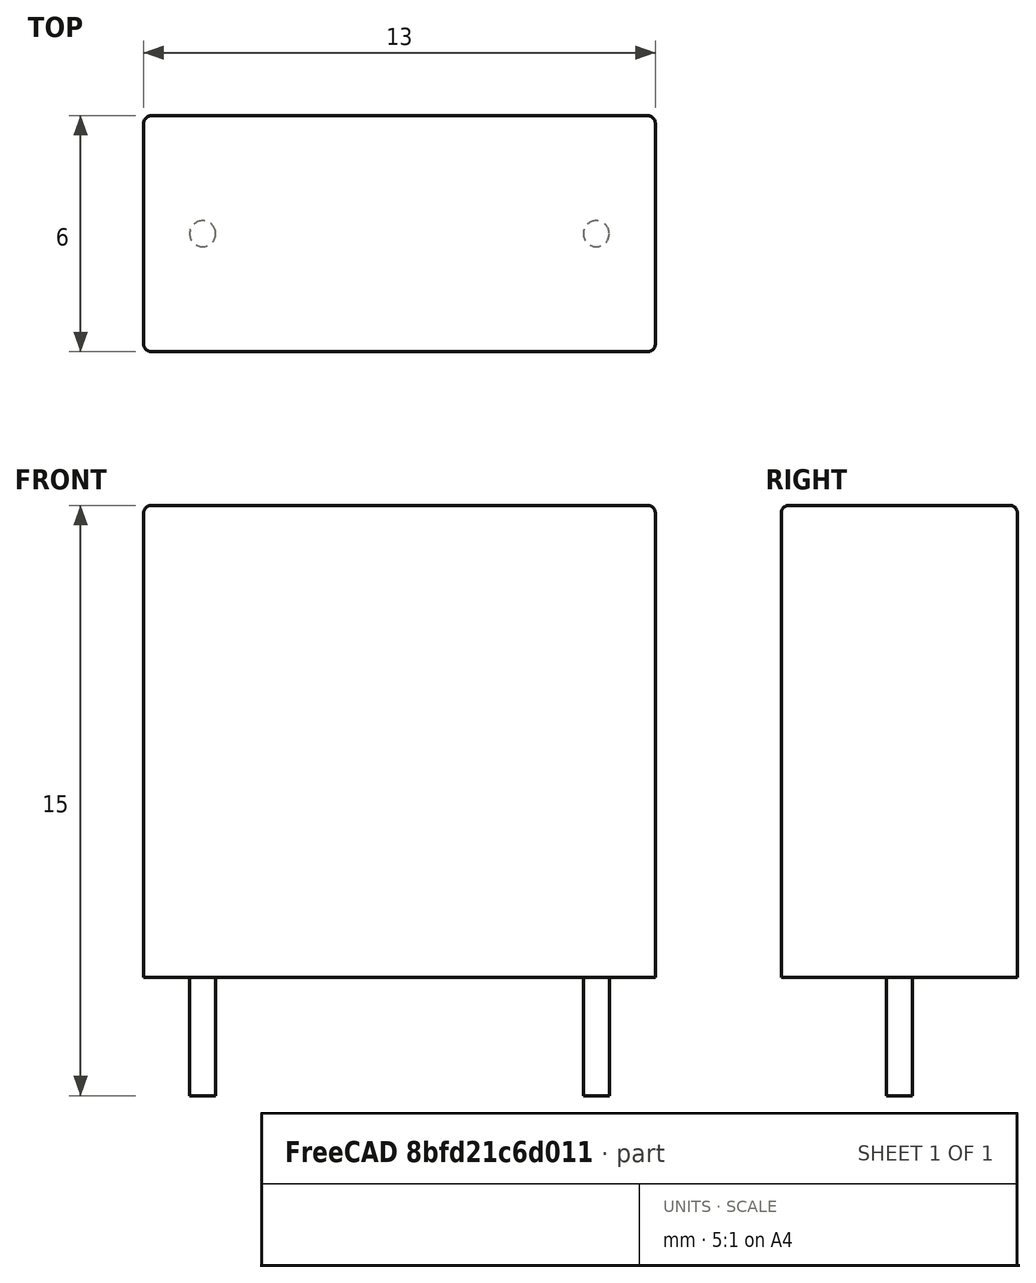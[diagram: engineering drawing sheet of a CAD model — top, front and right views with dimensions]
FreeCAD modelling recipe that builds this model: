
FCSTD DOCUMENT
Label: CAPARV1000W60L1300T600H1200
objects: Part::Cylinder×2, Part::Fuse×2, Part::Box×1, Part::Fillet×1
note: 6 computed .brp shape members not serialized (recipe doc carries the construction recipe); baked Part::Feature solids carry a one-line shape summary decoded from their .brp

FEATURE [Part::Cylinder] Cylinder  label="Pin1"
  Angle = 360
  Height = 3
  Placement = pos=(-5,0,-3) rot=(0,0,1;0rad)
  Radius = 0.33
FEATURE [Part::Cylinder] Cylinder001  label="Pin2"
  Angle = 360
  Height = 3
  Placement = pos=(5,0,-3) rot=(0,0,1;0rad)
  Radius = 0.33
FEATURE [Part::Box] Box  label="Grundkoerper"
  Height = 12
  Length = 13
  Placement = pos=(-6.5,-3,0) rot=(0,0,1;0rad)
  Width = 6
FEATURE [Part::Fillet] Fillet
  Base = -> Box
  Edges = 8 edges r=0.2: [Edge1,Edge2,Edge3,Edge5,Edge6,Edge7,Edge10,Edge12]
FEATURE [Part::Fuse] Fusion
  Base = -> Fillet
  Tool = -> Cylinder
FEATURE [Part::Fuse] Fusion001  label="CAPARV1000W60L1300T600H1200"
  Base = -> Fusion
  Tool = -> Cylinder001
